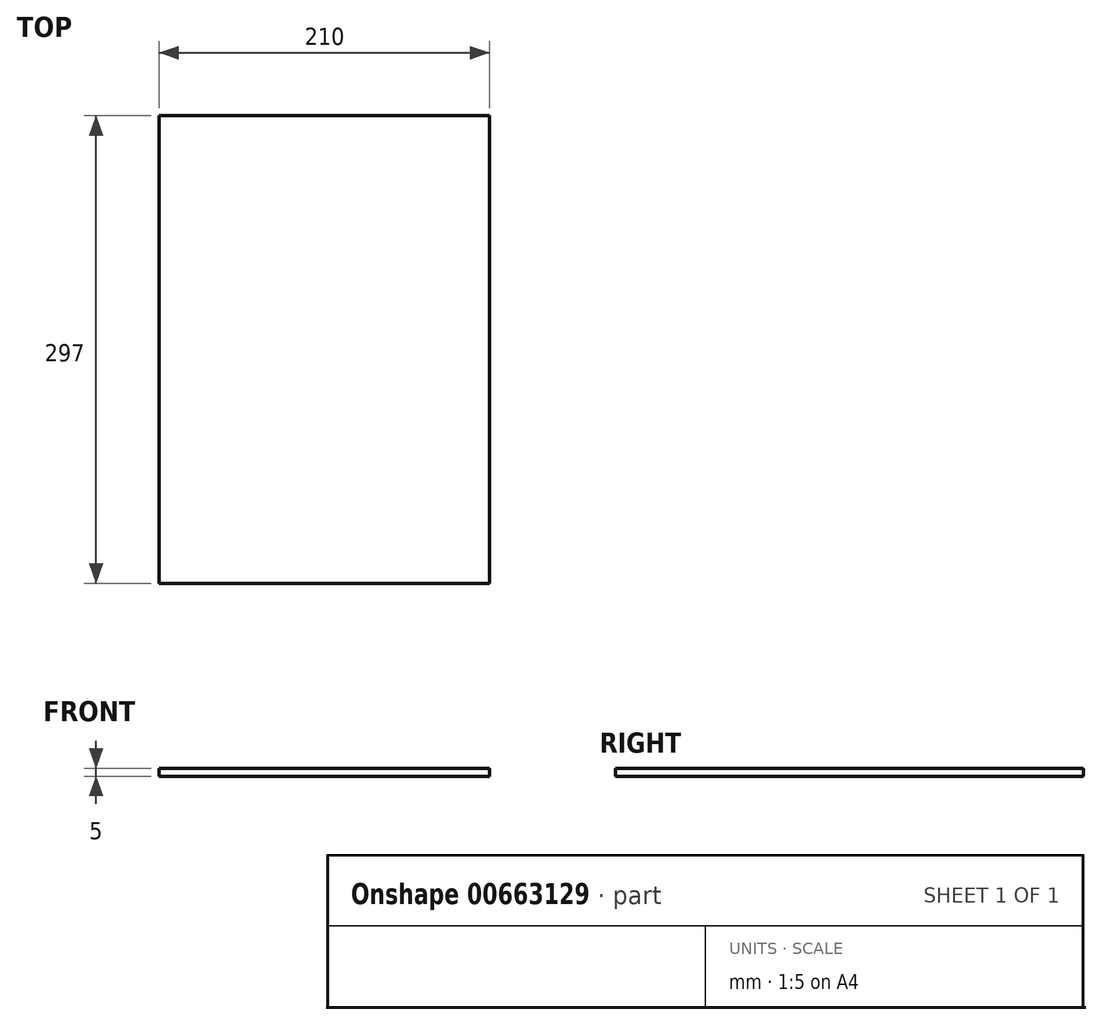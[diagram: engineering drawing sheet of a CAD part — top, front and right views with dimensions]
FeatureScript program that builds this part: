
annotation { "Feature Type Name" : "Feature", "Feature Type Description" : "" }
export const myFeature = defineFeature(function(context is Context, id is Id, definition is map)
    precondition{}
    {
        {
            var Q0;
            Q0=qCreatedBy(makeId("Top.planeOp"),FACE);
            var sketch = newSketch(context, id + "F0", { "sketchPlane" : qUnion([Q0])});
            skLineSegment(sketch, "E0.bottom", {"start": v(0, 0) * mm, "end": v(210, 0) * mm});
            skLineSegment(sketch, "E0.top", {"start": v(0, 297) * mm, "end": v(210, 297) * mm});
            skLineSegment(sketch, "E0.left", {"start": v(0, 0) * mm, "end": v(0, 297) * mm});
            skLineSegment(sketch, "E0.right", {"start": v(210, 0) * mm, "end": v(210, 297) * mm});
            skSolve(sketch);
        }
        {
            var Q0;
            Q0=makeQuery(id+"F0.imprint","IMPRINT",FACE,{"disambiguationData":[TD([[makeQuery(id+"F0.imprint","IMPRINT",EDGE,{"derivedFrom":sQuery(id+"F0.wireOp",EDGE,"E0.bottom")}),1.0]])]});
            extrude(context, id + "F1", {"entities" : qUnion([Q0]), "depth" : 5 * mm, "offsetDistance" : 25 * mm});
        }
    });
